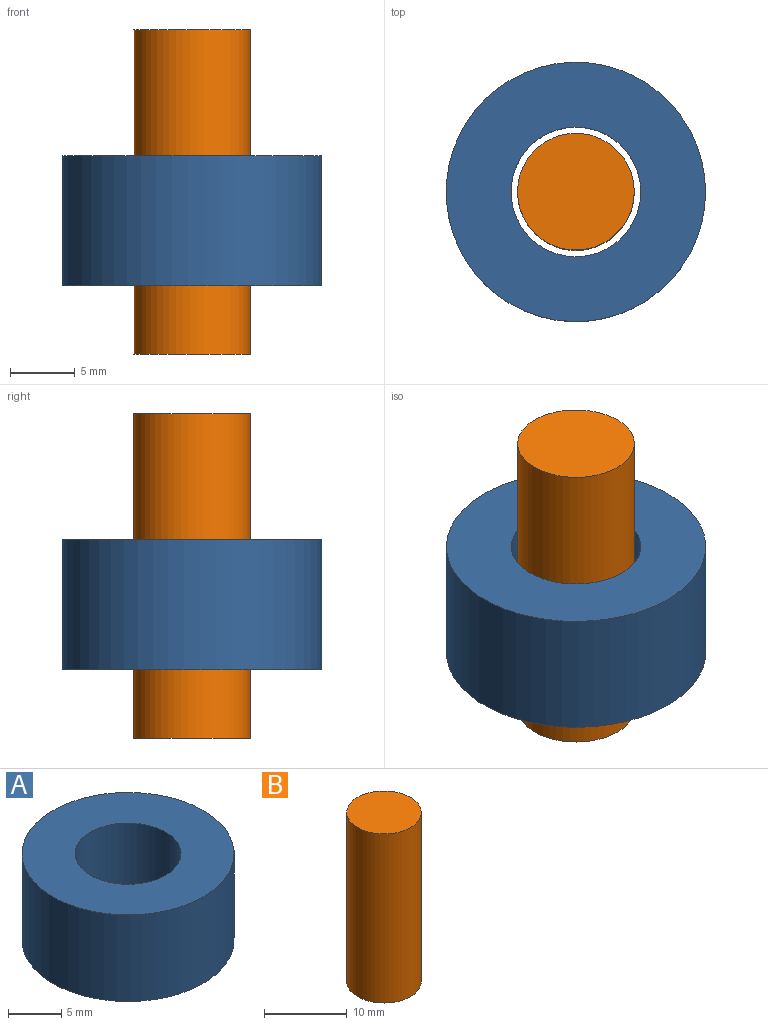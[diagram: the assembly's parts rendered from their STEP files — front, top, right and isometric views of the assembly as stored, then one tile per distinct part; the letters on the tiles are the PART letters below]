
ASSEMBLY  parts=2 mates=1
PART A: 4 faces, bbox 20x20x10 mm
  f0: cylinder r=5mm len=10mm, axis (0,0,-1), area 314.2mm2, adj f2,f3
  f1: cylinder r=10mm len=20mm, axis (0,0,-1), area 628.3mm2, adj f2,f3
  f2: plane 20x20mm, normal (0,0,1), area 235.6mm2, adj f0,f1
  f3: plane 20x20mm, normal (0,0,-1), area 235.6mm2, adj f0,f1
PART B: 3 faces, bbox 9x9x25 mm
  f0: cylinder r=4.5mm len=25mm, axis (0,0,-1), area 706.9mm2, adj f1,f2
  f1: plane 9x9mm, normal (0,0,1), area 63.6mm2, adj f0
  f2: plane 9x9mm, normal (0,0,-1), area 63.6mm2, adj f0
PLACE A t=(12.57,-16.77,6.59)mm fixed
PLACE B t=(26.46,-3.12,1.31)mm
MATE slider B.f0 <-> A.f0  axis (0,0,1) through (-13.46,-0.04,26.31)mm
